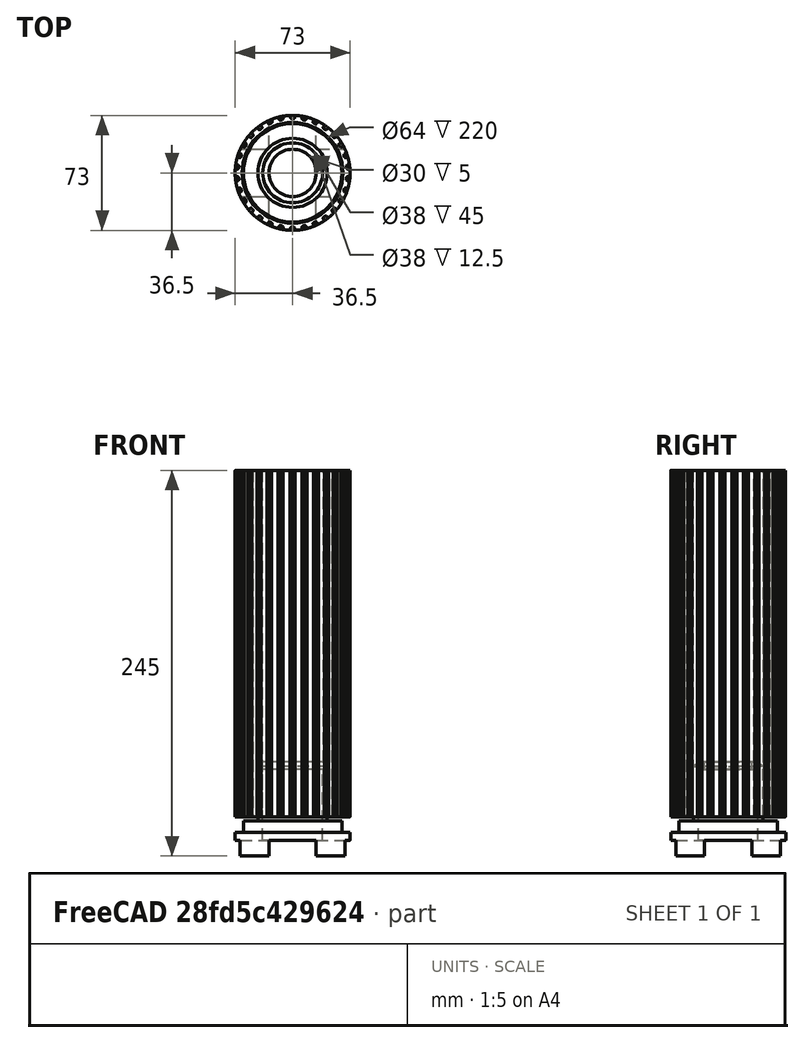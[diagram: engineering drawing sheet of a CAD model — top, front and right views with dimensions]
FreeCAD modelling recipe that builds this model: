
FCSTD DOCUMENT  (FreeCAD 0.15R4671 (Git))
Label: pica-small-v3
License: All rights reserved
LicenseURL: http://en.wikipedia.org/wiki/All_rights_reserved
objects: Drawing::FeatureView×10, Part::Cylinder×8, Part::Cut×7, Drawing::FeatureViewPart×6, Part::MultiFuse×5, Part::Box×4, Part::Part2DObjectPython×1, PartDesign::Pad×1, Drawing::FeaturePage×1, Part::Chamfer×1
note: 28 computed .brp shape members not serialized (recipe doc carries the construction recipe); baked Part::Feature solids carry a one-line shape summary decoded from their .brp

FEATURE [Part::Part2DObjectPython] InvoluteGear  # Draft 2D object (typed FeaturePython)
  ExternalGear = true
  HighPrecision = true
  Modules = 2.5
  NumberOfTeeth = 30
  PressureAngle = 20
FEATURE [PartDesign::Pad] Pad
  Length = 220
  Length2 = 100
  Sketch = -> InvoluteGear
  Type = 0
FEATURE [Part::Cylinder] Cylinder
  Angle = 360
  Height = 240
  Placement = pos=(0,0,-10) rot=(0,0,1;0rad)
  Radius = 32
FEATURE [Part::Cut] Cut  label="Final"
  Base = -> Pad
  Tool = -> Cylinder
FEATURE [Part::Cylinder] Cylinder001
  Angle = 360
  Height = 400
  Radius = 36.5
FEATURE [Part::Cylinder] Cylinder002
  Angle = 360
  Height = 400
  Radius = 100
FEATURE [Part::Cut] Cut001
  Base = -> Cylinder002
  Tool = -> Cylinder001
FEATURE [Part::Cut] Cut002  label="Shade"
  Base = -> Cut
  Placement = pos=(0,0,25) rot=(0,0,1;0rad)
  Tool = -> Cut001
FEATURE [Part::Cylinder] Cylinder003
  Angle = 360
  Height = 15
  Radius = 36.5
FEATURE [Part::Cylinder] Cylinder004
  Angle = 360
  Height = 22.5
  Radius = 31.3
FEATURE [Part::MultiFuse] Fusion  label="Base Fusion"
  Shapes = -> [Cylinder004,Cylinder003]
FEATURE [Part::Box] Box  label="Cube"
  Height = 10
  Length = 100
  Placement = pos=(-50,-15,0) rot=(0,0,1;0rad)
  Width = 30
FEATURE [Part::Box] Box001  label="Cube001"
  Height = 10
  Length = 100
  Placement = pos=(15,-50,0) rot=(0,0,1;1.5708rad)
  Width = 30
FEATURE [Part::MultiFuse] Fusion001  label="Feet Cutout Fusion"
  Shapes = -> [Box001,Box]
FEATURE [Drawing::FeatureViewPart] FrontView  label="Shade Side"
  Direction = (0,-1,0)
  HiddenWidth = 0.15
  LineWidth = 0.35
  Rotation = 90
  ShowHiddenLines = true
  ShowSmoothLines = false
  Source = -> Cut002
  Tolerance = 0.05
  ViewResult = <blob: 104580 chars omitted>
  Visible = true
  X = 80
  Y = 270
FEATURE [Drawing::FeatureViewPart] View001  label="Shade Top"
  Direction = (0,0,1)
  HiddenWidth = 0.15
  LineWidth = 0.35
  Rotation = 0
  ShowHiddenLines = false
  ShowSmoothLines = false
  Source = -> Cut002
  Tolerance = 0.05
  ViewResult = <blob: 17501 chars omitted>
  Visible = true
  X = 300
  Y = 80
FEATURE [Drawing::FeatureView] dim006  label="Base Radius"
  Rotation = 0
  ViewResult = <g   >\n <circle cx ="300.000000" cy ="170.000000" r="0.500000" stroke="none" fill="rgb(0,0,0)" /> \n<line x1="255.718312" y1="135.631286" x2="300.000000" y2="170.000000" style="stroke:rgb(0,0,0);stroke-width:0.30" />\n<polygon points="275.273643,150.808927 277.030448,153.438307 278.433561,153.261461 278.256715,151.858348" style="fill:rgb(0,0,0);stroke:rgb(0,0,0);stroke-width:0" />\n<line x1="255.718312" y1="135.631286" x2="231.639949" y2="135.631286" style="stroke:rgb(0,0,0);stroke-width:0.30" />\n<text x="219.448373" y="136.850443" font-family="Arial" font-size="3.6" fill="rgb(0,0,0)" text-anchor="inherit"  >R31.3</text>\n<!--31.3-->\n<!--R%3.3f-->\n</g> 
  Visible = true
  X = 0
  Y = 0
FEATURE [Drawing::FeatureView] centerLines
  Rotation = 0
  ViewResult = <g  transform="scale(1.000000,1.000000)" stroke="rgb(0,0,0)"  stroke-width="0.300000" >\n<path d="M 300.000000,170.000000 L 300.000000,168.000000 M 300.000000,166.000000 L 300.000000,160.000000 M 300.000000,158.000000 L 300.000000,156.000000 "/>\n<path d="M 300.000000,170.000000 L 302.000000,170.000000 M 304.000000,170.000000 L 310.000000,170.000000 M 312.000000,170.000000 L 314.000000,170.000000 "/>\n<path d="M 300.000000,170.000000 L 300.000000,172.000000 M 300.000000,174.000000 L 300.000000,180.000000 M 300.000000,182.000000 L 300.000000,184.000000 "/>\n<path d="M 300.000000,170.000000 L 298.000000,170.000000 M 296.000000,170.000000 L 290.000000,170.000000 M 288.000000,170.000000 L 286.000000,170.000000 "/>\n</g> 
  Visible = true
  X = 0
  Y = 0
FEATURE [Drawing::FeatureView] centerLines001
  Rotation = 0
  ViewResult = <g  transform="scale(1.000000,1.000000)" stroke="rgb(0,0,0)"  stroke-width="0.300000" >\n<path d="M 300.000000,80.000000 L 300.000000,82.000000 M 300.000000,84.000000 L 300.000000,90.000000 M 300.000000,92.000000 L 300.000000,94.000000 "/>\n<path d="M 300.000000,80.000000 L 302.000000,80.000000 M 304.000000,80.000000 L 310.000000,80.000000 M 312.000000,80.000000 L 314.000000,80.000000 "/>\n<path d="M 300.000000,80.000000 L 300.000000,78.000000 M 300.000000,76.000000 L 300.000000,70.000000 M 300.000000,68.000000 L 300.000000,66.000000 "/>\n<path d="M 300.000000,80.000000 L 298.000000,80.000000 M 296.000000,80.000000 L 290.000000,80.000000 M 288.000000,80.000000 L 286.000000,80.000000 "/>\n</g> 
  Visible = true
  X = 0
  Y = 0
FEATURE [Drawing::FeatureView] dim007  label="Shade Radius"
  Rotation = 0
  ViewResult = <g   >\n <circle cx ="300.000000" cy ="80.000000" r="0.500000" stroke="none" fill="rgb(0,0,0)" /> \n<line x1="340.917441" y1="111.884102" x2="300.000000" y2="80.000000" style="stroke:rgb(0,0,0);stroke-width:0.30" />\n<polygon points="325.241495,99.668933 323.489759,97.036174 322.086308,97.210316 322.260451,98.613767" style="fill:rgb(0,0,0);stroke:rgb(0,0,0);stroke-width:0" />\n<line x1="340.917441" y1="111.884102" x2="365.557939" y2="111.884102" style="stroke:rgb(0,0,0);stroke-width:0.30" />\n<text x="369.473360" y="112.835313" font-family="Arial" font-size="3.6" fill="rgb(0,0,0)" text-anchor="inherit"  >R32</text>\n<!--32.0-->\n<!--R%3.3f-->\n</g> 
  Visible = true
  X = 0
  Y = 0
FEATURE [Part::Cylinder] Cylinder005
  Angle = 360
  Height = 90
  Radius = 15
FEATURE [Part::Cylinder] Cylinder006
  Angle = 360
  Height = 55
  Radius = 19
FEATURE [Part::MultiFuse] Fusion002  label="Fixture Mount"
  Shapes = -> [Cylinder005,Cylinder006]
FEATURE [Drawing::FeatureViewPart] View004  label="Base Top"
  Direction = (0,0,1)
  HiddenWidth = 0.15
  LineWidth = 0.35
  Rotation = 0
  ShowHiddenLines = false
  ShowSmoothLines = false
  Tolerance = 0.05
  ViewResult = <g id="Base Top"\n   transform="rotate(0,300,170) translate(300,170) scale(1,1)"\n  >\n<g   stroke="rgb(0, 0, 0)"\n   stroke-width="0.35"\n   stroke-linecap="butt"\n   stroke-linejoin="miter"\n   fill="none"\n   transform="scale(1,-1)"\n  >\n<circle cx ="0" cy ="0" r ="23.3" /><circle cx ="0" cy ="0" r ="15" /><circle cx ="0" cy ="0" r ="31.3" /><circle cx ="0" cy ="0" r ="36.5" /></g>\n</g>
  Visible = true
  X = 300
  Y = 170
FEATURE [Drawing::FeatureViewPart] View005  label="Base Side"
  Direction = (0,-1,0)
  HiddenWidth = 0.15
  LineWidth = 0.35
  Rotation = 90
  ShowHiddenLines = false
  ShowSmoothLines = false
  Tolerance = 0.05
  ViewResult = <blob: 2600 chars omitted>
  Visible = true
  X = 80
  Y = 270
FEATURE [Drawing::FeatureViewPart] View  label="Base Side001"
  Direction = (0,-1,0)
  HiddenWidth = 0.15
  LineWidth = 0.35
  Rotation = 90
  ShowHiddenLines = false
  ShowSmoothLines = false
  Tolerance = 0.05
  ViewResult = <blob: 2605 chars omitted>
  Visible = true
  X = 180
  Y = 100
FEATURE [Drawing::FeatureViewPart] View006  label="Base Top001"
  Direction = (0,0,-1)
  HiddenWidth = 0.15
  LineWidth = 0.35
  Rotation = 0
  ShowHiddenLines = false
  ShowSmoothLines = false
  Tolerance = 0.05
  ViewResult = <blob: 2659 chars omitted>
  Visible = true
  X = 180
  Y = 170
FEATURE [Drawing::FeatureView] dim010  label="dim001"
  Rotation = 0
  ViewResult = <g   >\n<line x1="158.500000" y1="235.000000" x2="177.679727" y2="235.000000" style="stroke:rgb(0,0,0);stroke-width:0.30" />\n<line x1="158.483300" y1="250.000000" x2="177.679727" y2="250.000000" style="stroke:rgb(0,0,0);stroke-width:0.30" />\n<line x1="176.679727" y1="235.000000" x2="176.679727" y2="250.000000" style="stroke:rgb(0,0,0);stroke-width:0.30" />\n<polygon points="176.679727,235.000000 175.679727,238.000000 176.679727,239.000000 177.679727,238.000000" style="fill:rgb(0,0,0);stroke:rgb(0,0,0);stroke-width:0" /><polygon points="176.679727,250.000000 177.679727,247.000000 176.679727,246.000000 175.679727,247.000000" style="fill:rgb(0,0,0);stroke:rgb(0,0,0);stroke-width:0" />\n<text x="183.587709" y="244.783611" font-family="Arial" font-size="3.6" fill="rgb(0,0,0)" text-anchor="inherit" transform="rotate(-90.000000 183.587709,244.783611)" >15</text>\n</g> 
  Visible = true
  X = 0
  Y = 0
FEATURE [Drawing::FeatureView] dim011  label="dim002"
  Rotation = 0
  ViewResult = <g   >\n<line x1="153.300000" y1="228.000000" x2="177.810311" y2="228.000000" style="stroke:rgb(0,0,0);stroke-width:0.30" />\n<line x1="158.500000" y1="235.000000" x2="177.810311" y2="235.000000" style="stroke:rgb(0,0,0);stroke-width:0.30" />\n<line x1="176.810311" y1="228.000000" x2="176.810311" y2="235.000000" style="stroke:rgb(0,0,0);stroke-width:0.30" />\n<polygon points="176.810311,228.000000 177.810311,225.000000 176.810311,224.000000 175.810311,225.000000" style="fill:rgb(0,0,0);stroke:rgb(0,0,0);stroke-width:0" /><polygon points="176.810311,235.000000 175.810311,238.000000 176.810311,239.000000 177.810311,238.000000" style="fill:rgb(0,0,0);stroke:rgb(0,0,0);stroke-width:0" />\n<text x="183.208911" y="232.569545" font-family="Arial" font-size="3.6" fill="rgb(0,0,0)" text-anchor="inherit" transform="rotate(-90.000000 183.208911,232.569545)" >7</text>\n</g> 
  Visible = true
  X = 0
  Y = 0
FEATURE [Drawing::FeatureView] centerLines004
  Rotation = 0
  ViewResult = <g  transform="scale(1.000000,1.000000)" stroke="rgb(0,0,0)"  stroke-width="0.300000" >\n<path d="M 180.000000,169.999925 L 180.000000,167.999925 M 180.000000,165.999925 L 180.000000,159.999925 M 180.000000,157.999925 L 180.000000,155.999925 "/>\n<path d="M 180.000000,169.999925 L 182.000000,169.999925 M 184.000000,169.999925 L 190.000000,169.999925 M 192.000000,169.999925 L 194.000000,169.999925 "/>\n<path d="M 180.000000,169.999925 L 180.000000,171.999925 M 180.000000,173.999925 L 180.000000,179.999925 M 180.000000,181.999925 L 180.000000,183.999925 M 180.000000,185.999925 L 180.000000,186.160469 "/>\n<path d="M 180.000000,169.999925 L 178.000000,169.999925 M 176.000000,169.999925 L 170.000000,169.999925 M 168.000000,169.999925 L 166.583365,169.999925 "/>\n</g> 
  Visible = true
  X = 0
  Y = 0
FEATURE [Drawing::FeatureView] dim
  Rotation = 0
  ViewResult = <g   >\n<line x1="41.500000" y1="25.000000" x2="33.944194" y2="25.000000" style="stroke:rgb(0,0,0);stroke-width:0.30" />\n<line x1="41.500000" y1="245.000000" x2="33.944194" y2="245.000000" style="stroke:rgb(0,0,0);stroke-width:0.30" />\n<line x1="34.944194" y1="25.000000" x2="34.944194" y2="245.000000" style="stroke:rgb(0,0,0);stroke-width:0.30" />\n<polygon points="34.944194,25.000000 33.944194,28.000000 34.944194,29.000000 35.944194,28.000000" style="fill:rgb(0,0,0);stroke:rgb(0,0,0);stroke-width:0" /><polygon points="34.944194,245.000000 35.944194,242.000000 34.944194,241.000000 33.944194,242.000000" style="fill:rgb(0,0,0);stroke:rgb(0,0,0);stroke-width:0" />\n<text x="31.608126" y="136.256650" font-family="Arial" font-size="3.6" fill="rgb(0,0,0)" text-anchor="inherit" transform="rotate(-90.000000 31.608126,136.256650)" >220</text>\n</g> 
  Visible = true
  X = 0
  Y = 0
FEATURE [Drawing::FeatureView] dim012
  Rotation = 0
  ViewResult = <g   >\n<line x1="118.122400" y1="245.000000" x2="126.861722" y2="245.000000" style="stroke:rgb(0,0,0);stroke-width:0.30" />\n<line x1="115.275400" y1="270.000000" x2="126.861722" y2="270.000000" style="stroke:rgb(0,0,0);stroke-width:0.30" />\n<line x1="125.861722" y1="245.000000" x2="125.861722" y2="270.000000" style="stroke:rgb(0,0,0);stroke-width:0.30" />\n<polygon points="125.861722,245.000000 124.861722,248.000000 125.861722,249.000000 126.861722,248.000000" style="fill:rgb(0,0,0);stroke:rgb(0,0,0);stroke-width:0" /><polygon points="125.861722,270.000000 126.861722,267.000000 125.861722,266.000000 124.861722,267.000000" style="fill:rgb(0,0,0);stroke:rgb(0,0,0);stroke-width:0" />\n<text x="132.056471" y="260.197520" font-family="Arial" font-size="3.6" fill="rgb(0,0,0)" text-anchor="inherit" transform="rotate(-90.000000 132.056471,260.197520)" >25</text>\n</g> 
  Visible = true
  X = 0
  Y = 0
FEATURE [Drawing::FeatureView] dim013
  Rotation = 0
  ViewResult = <g   >\n<line x1="143.500000" y1="73.000000" x2="143.500000" y2="45.465562" style="stroke:rgb(0,0,0);stroke-width:0.30" />\n<line x1="216.500000" y1="73.000000" x2="216.500000" y2="45.465562" style="stroke:rgb(0,0,0);stroke-width:0.30" />\n<line x1="143.500000" y1="46.465562" x2="216.500000" y2="46.465562" style="stroke:rgb(0,0,0);stroke-width:0.30" />\n<polygon points="143.500000,46.465562 146.500000,47.465562 147.500000,46.465562 146.500000,45.465562" style="fill:rgb(0,0,0);stroke:rgb(0,0,0);stroke-width:0" /><polygon points="216.500000,46.465562 213.500000,45.465562 212.500000,46.465562 213.500000,47.465562" style="fill:rgb(0,0,0);stroke:rgb(0,0,0);stroke-width:0" />\n<text x="177.413963" y="43.541156" font-family="Arial" font-size="3.6" fill="rgb(0,0,0)" text-anchor="inherit" transform="rotate(0.000000 177.413963,43.541156)" >73</text>\n</g> 
  Visible = true
  X = 0
  Y = 0
FEATURE [Drawing::FeaturePage] AutoDrawing  label="Initial Sketch"
  EditableTexts = FLOYD DIEBEL | 8/22/2015 | 1:1 | 1 | 1 | PICA (SMALL V2) | LAMP WITH SHADE
  Group = -> [FrontView,View001,dim006,centerLines,centerLines001,dim007,View004,View005,dim010,dim011,View,View006,centerLines004,dim,dim012,dim013]
  Template = C:/Program Files/FreeCAD 0.15/data/Mod/Drawing/Templates/A3_Landscape.svg
FEATURE [Part::Cylinder] Cylinder007
  Angle = 360
  Height = 60
  Radius = 22
FEATURE [Part::MultiFuse] Fusion003
  Shapes = -> [Fusion,Cylinder007]
FEATURE [Part::Cut] Cut005  label="Raw"
  Base = -> Fusion003
  Tool = -> Fusion002
FEATURE [Part::Cut] Cut003  label="Plain Base"
  Base = -> Fusion
  Tool = -> Fusion001
FEATURE [Part::Cut] Cut004  label="Base w/ Mount"
  Base = -> Cut003
  Tool = -> Fusion002
FEATURE [Part::Box] Box002  label="Cube002"
  Height = 10
  Length = 100
  Placement = pos=(-50,-15,0) rot=(0,0,1;0rad)
  Width = 30
FEATURE [Part::Box] Box003  label="Cube003"
  Height = 10
  Length = 100
  Placement = pos=(15,-50,0) rot=(0,0,1;1.5708rad)
  Width = 30
FEATURE [Part::MultiFuse] Fusion004  label="Feet Cutout Fusion001"
  Shapes = -> [Box003,Box002]
FEATURE [Part::Cut] Cut006  label="Pre-chamfer"
  Base = -> Cut005
  Tool = -> Fusion004
FEATURE [Part::Chamfer] Chamfer
  Base = -> Cut006
  Edges = 1 edges r=3: [Edge1]
